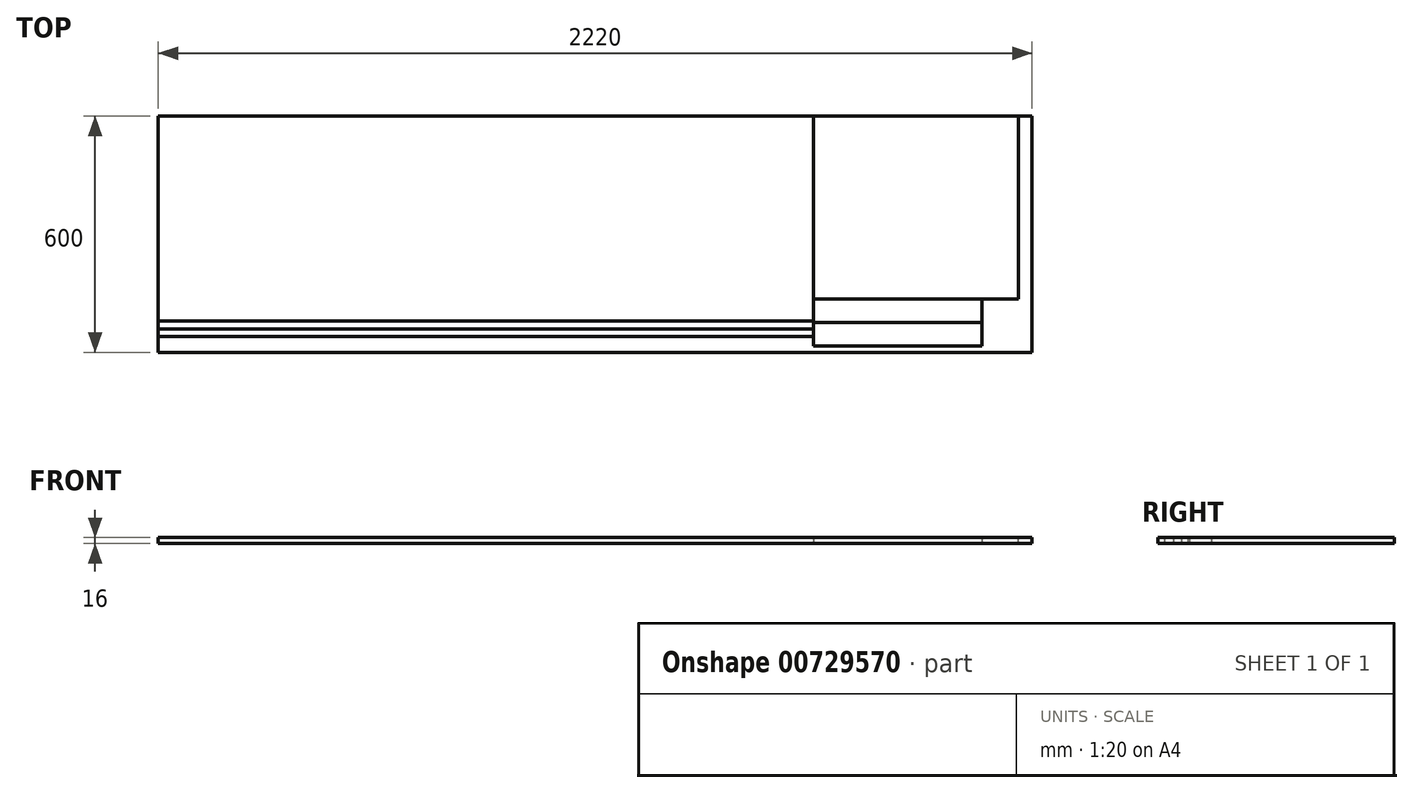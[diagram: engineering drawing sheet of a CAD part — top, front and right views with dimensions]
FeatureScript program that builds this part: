
annotation { "Feature Type Name" : "Feature", "Feature Type Description" : "" }
export const myFeature = defineFeature(function(context is Context, id is Id, definition is map)
    precondition{}
    {
        {
            var Q0;
            Q0=qCreatedBy(makeId("Top.planeOp"),FACE);
            var sketch = newSketch(context, id + "F0", { "sketchPlane" : qUnion([Q0])});
            skLineSegment(sketch, "E0.bottom", {"start": v(1110, -300) * mm, "end": v(-1110, -300) * mm});
            skLineSegment(sketch, "E0.top", {"start": v(1110, 300) * mm, "end": v(-1110, 300) * mm});
            skLineSegment(sketch, "E0.left", {"start": v(1110, -300) * mm, "end": v(1110, 300) * mm});
            skLineSegment(sketch, "E0.right", {"start": v(-1110, -300) * mm, "end": v(-1110, 300) * mm});
            skPoint(sketch, "E0.middle", {"position": v(0, 0) * mm});
            skSolve(sketch);
        }
        {
            var Q0;
            Q0=makeQuery(id+"F0.imprint","IMPRINT",FACE,{"disambiguationData":[TD([[makeQuery(id+"F0.imprint","IMPRINT",EDGE,{"derivedFrom":sQuery(id+"F0.wireOp",EDGE,"E0.bottom")}),-1.0]])]});
            extrude(context, id + "F1", {"entities" : qUnion([Q0]), "depth" : 16 * mm, "offsetDistance" : 25 * mm});
        }
        {
            var Q0;
            Q0=makeQuery(id+"F1.opExtrude","CAP_FACE",FACE,{"disambiguationData":[OSD([sQuery(id+"F0.wireOp",EDGE,"E0.bottom"),sQuery(id+"F0.wireOp",EDGE,"E0.top"),sQuery(id+"F0.wireOp",EDGE,"E0.left"),sQuery(id+"F0.wireOp",EDGE,"E0.right")])],"isStart":false});
            var sketch = newSketch(context, id + "F2", { "sketchPlane" : qUnion([Q0])});
            skLineSegment(sketch, "E1.bottom", {"start": v(-1110, 300) * mm, "end": v(555, 300) * mm});
            skLineSegment(sketch, "E1.top", {"start": v(-1110, -220) * mm, "end": v(555, -220) * mm});
            skLineSegment(sketch, "E1.left", {"start": v(-1110, 300) * mm, "end": v(-1110, -220) * mm});
            skLineSegment(sketch, "E1.right", {"start": v(555, 300) * mm, "end": v(555, -220) * mm});
            skSolve(sketch);
        }
        {
            var Q0;
            Q0=makeQuery(id+"F2.imprint","IMPRINT",FACE,{"disambiguationData":[TD([[makeQuery(id+"F2.imprint","IMPRINT",EDGE,{"derivedFrom":sQuery(id+"F2.wireOp",EDGE,"E1.bottom")}),1.0]])]});
            extrude(context, id + "F3", {"entities" : qUnion([Q0]), "oppositeDirection" : true, "depth" : 16 * mm, "offsetDistance" : 25 * mm});
        }
        {
            var Q0;
            Q0=makeQuery(id+"F1.opExtrude","CAP_FACE",FACE,{"disambiguationData":[OSD([sQuery(id+"F0.wireOp",EDGE,"E0.bottom"),sQuery(id+"F0.wireOp",EDGE,"E0.top"),sQuery(id+"F0.wireOp",EDGE,"E0.left"),sQuery(id+"F0.wireOp",EDGE,"E0.right")])],"isStart":true});
            var sketch = newSketch(context, id + "F4", { "sketchPlane" : qUnion([Q0])});
            skPoint(sketch, "E2.0", {"position": v(-1110, 220) * mm});
            skLineSegment(sketch, "E3.bottom", {"start": v(-1110, 220) * mm, "end": v(555, 220) * mm});
            skLineSegment(sketch, "E3.top", {"start": v(-1110, 240) * mm, "end": v(555, 240) * mm});
            skLineSegment(sketch, "E3.left", {"start": v(-1110, 220) * mm, "end": v(-1110, 240) * mm});
            skLineSegment(sketch, "E3.right", {"start": v(555, 220) * mm, "end": v(555, 240) * mm});
            skSolve(sketch);
        }
        {
            var Q0;
            Q0=makeQuery(id+"F4.imprint","IMPRINT",FACE,{"disambiguationData":[TD([[makeQuery(id+"F4.imprint","IMPRINT",EDGE,{"derivedFrom":sQuery(id+"F4.wireOp",EDGE,"E3.bottom")}),1.0]])]});
            extrude(context, id + "F5", {"entities" : qUnion([Q0]), "oppositeDirection" : true, "depth" : 16 * mm, "offsetDistance" : 25 * mm});
        }
        {
            var Q0;
            Q0=makeQuery(id+"F1.opExtrude","CAP_FACE",FACE,{"disambiguationData":[OSD([sQuery(id+"F0.wireOp",EDGE,"E0.bottom"),sQuery(id+"F0.wireOp",EDGE,"E0.top"),sQuery(id+"F0.wireOp",EDGE,"E0.left"),sQuery(id+"F0.wireOp",EDGE,"E0.right")])],"isStart":false});
            var sketch = newSketch(context, id + "F6", { "sketchPlane" : qUnion([Q0])});
            skPoint(sketch, "E4.0", {"position": v(-1110, -240) * mm});
            skLineSegment(sketch, "E5.bottom", {"start": v(-1110, -240) * mm, "end": v(555, -240) * mm});
            skLineSegment(sketch, "E5.top", {"start": v(-1110, -260) * mm, "end": v(555, -260) * mm});
            skLineSegment(sketch, "E5.left", {"start": v(-1110, -240) * mm, "end": v(-1110, -260) * mm});
            skLineSegment(sketch, "E5.right", {"start": v(555, -240) * mm, "end": v(555, -260) * mm});
            skSolve(sketch);
        }
        {
            var Q0;
            Q0=makeQuery(id+"F6.imprint","IMPRINT",FACE,{"disambiguationData":[TD([[makeQuery(id+"F6.imprint","IMPRINT",EDGE,{"derivedFrom":sQuery(id+"F6.wireOp",EDGE,"E5.bottom")}),-1.0]])]});
            extrude(context, id + "F7", {"entities" : qUnion([Q0]), "oppositeDirection" : true, "depth" : 16 * mm, "offsetDistance" : 25 * mm});
        }
        {
            var Q0;
            Q0=makeQuery(id+"F1.opExtrude","CAP_FACE",FACE,{"disambiguationData":[OSD([sQuery(id+"F0.wireOp",EDGE,"E0.bottom"),sQuery(id+"F0.wireOp",EDGE,"E0.top"),sQuery(id+"F0.wireOp",EDGE,"E0.left"),sQuery(id+"F0.wireOp",EDGE,"E0.right")])],"isStart":false});
            var sketch = newSketch(context, id + "F8", { "sketchPlane" : qUnion([Q0])});
            skPoint(sketch, "E6.0", {"position": v(555, 300) * mm});
            skLineSegment(sketch, "E7.bottom", {"start": v(555, 300) * mm, "end": v(1075, 300) * mm});
            skLineSegment(sketch, "E7.top", {"start": v(555, -164) * mm, "end": v(1075, -164) * mm});
            skLineSegment(sketch, "E7.left", {"start": v(555, 300) * mm, "end": v(555, -164) * mm});
            skLineSegment(sketch, "E7.right", {"start": v(1075, 300) * mm, "end": v(1075, -164) * mm});
            skSolve(sketch);
        }
        {
            var Q0;
            Q0=makeQuery(id+"F8.imprint","IMPRINT",FACE,{"disambiguationData":[TD([[makeQuery(id+"F8.imprint","IMPRINT",EDGE,{"derivedFrom":sQuery(id+"F8.wireOp",EDGE,"E7.bottom")}),1.0]])]});
            extrude(context, id + "F9", {"entities" : qUnion([Q0]), "oppositeDirection" : true, "depth" : 16 * mm, "offsetDistance" : 25 * mm});
        }
        {
            var Q0;
            Q0=makeQuery(id+"F1.opExtrude","CAP_FACE",FACE,{"disambiguationData":[OSD([sQuery(id+"F0.wireOp",EDGE,"E0.bottom"),sQuery(id+"F0.wireOp",EDGE,"E0.top"),sQuery(id+"F0.wireOp",EDGE,"E0.left"),sQuery(id+"F0.wireOp",EDGE,"E0.right")])],"isStart":true});
            var sketch = newSketch(context, id + "F10", { "sketchPlane" : qUnion([Q0])});
            skPoint(sketch, "E8.0", {"position": v(555, 164) * mm});
            skLineSegment(sketch, "E9.bottom", {"start": v(555, 164) * mm, "end": v(983, 164) * mm});
            skLineSegment(sketch, "E9.top", {"start": v(555, 224) * mm, "end": v(983, 224) * mm});
            skLineSegment(sketch, "E9.left", {"start": v(555, 164) * mm, "end": v(555, 224) * mm});
            skLineSegment(sketch, "E9.right", {"start": v(983, 164) * mm, "end": v(983, 224) * mm});
            skSolve(sketch);
        }
        {
            var Q0;
            Q0=makeQuery(id+"F10.imprint","IMPRINT",FACE,{"disambiguationData":[TD([[makeQuery(id+"F10.imprint","IMPRINT",EDGE,{"derivedFrom":sQuery(id+"F10.wireOp",EDGE,"E9.bottom")}),1.0]])]});
            extrude(context, id + "F11", {"entities" : qUnion([Q0]), "oppositeDirection" : true, "depth" : 16 * mm, "offsetDistance" : 25 * mm});
        }
        {
            var Q0;
            Q0=makeQuery(id+"F1.opExtrude","CAP_FACE",FACE,{"disambiguationData":[OSD([sQuery(id+"F0.wireOp",EDGE,"E0.bottom"),sQuery(id+"F0.wireOp",EDGE,"E0.top"),sQuery(id+"F0.wireOp",EDGE,"E0.left"),sQuery(id+"F0.wireOp",EDGE,"E0.right")])],"isStart":true});
            var sketch = newSketch(context, id + "F12", { "sketchPlane" : qUnion([Q0])});
            skPoint(sketch, "E10.0", {"position": v(555, 224) * mm});
            skLineSegment(sketch, "E11.bottom", {"start": v(555, 224) * mm, "end": v(983, 224) * mm});
            skLineSegment(sketch, "E11.top", {"start": v(555, 284) * mm, "end": v(983, 284) * mm});
            skLineSegment(sketch, "E11.left", {"start": v(555, 224) * mm, "end": v(555, 284) * mm});
            skLineSegment(sketch, "E11.right", {"start": v(983, 224) * mm, "end": v(983, 284) * mm});
            skSolve(sketch);
        }
        {
            var Q0;
            Q0=makeQuery(id+"F12.imprint","IMPRINT",FACE,{"disambiguationData":[TD([[makeQuery(id+"F12.imprint","IMPRINT",EDGE,{"derivedFrom":sQuery(id+"F12.wireOp",EDGE,"E11.bottom")}),1.0]])]});
            extrude(context, id + "F13", {"entities" : qUnion([Q0]), "oppositeDirection" : true, "depth" : 16 * mm, "offsetDistance" : 25 * mm});
        }
    });
